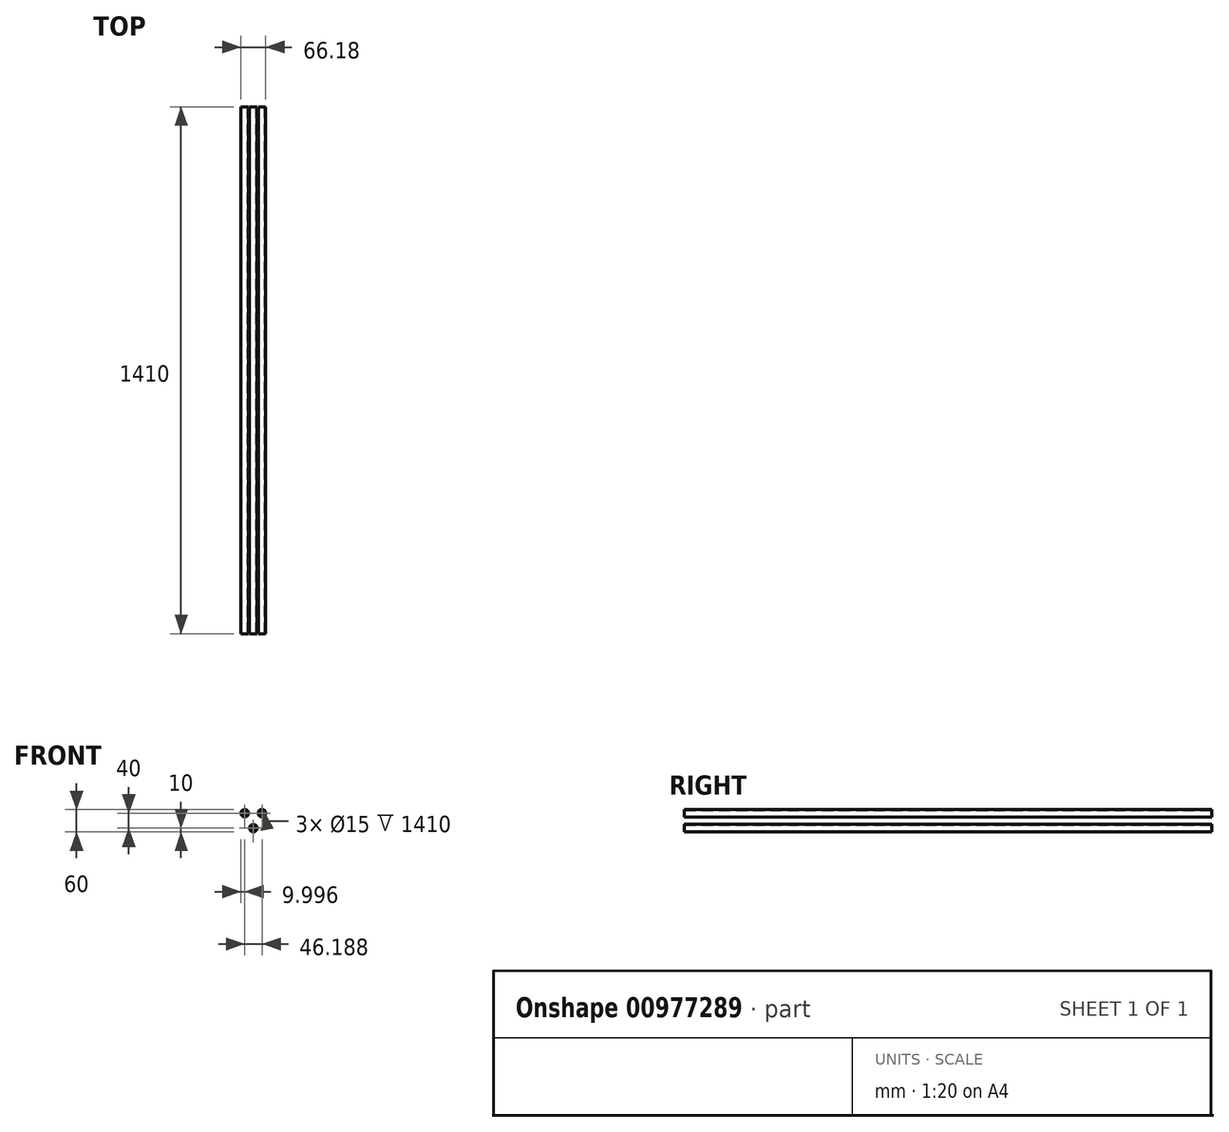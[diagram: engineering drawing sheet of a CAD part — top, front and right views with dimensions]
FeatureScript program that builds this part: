
annotation { "Feature Type Name" : "Feature", "Feature Type Description" : "" }
export const myFeature = defineFeature(function(context is Context, id is Id, definition is map)
    precondition{}
    {
        {
            var Q0;
            Q0=qCreatedBy(makeId("Front.planeOp"),FACE);
            var sketch = newSketch(context, id + "F0", { "sketchPlane" : qUnion([Q0])});
            skCircle(sketch, "E0", {"center": v(0, 0) * mm, "radius": 10 * mm});
            skCircle(sketch, "E1", {"center": v(23.1, 40) * mm, "radius": 10 * mm});
            skCircle(sketch, "E2", {"center": v(-23.1, 40) * mm, "radius": 10 * mm});
            skCircle(sketch, "E3", {"center": v(-23.1, 40) * mm, "radius": 15 * mm});
            skCircle(sketch, "E4", {"center": v(23.1, 40) * mm, "radius": 15 * mm});
            skCircle(sketch, "E5", {"center": v(0, 0) * mm, "radius": 15 * mm});
            skLineSegment(sketch, "E6", {"start": v(0, 0) * mm, "end": v(-23.1, 40) * mm});
            skLineSegment(sketch, "E7", {"start": v(23.1, 40) * mm, "end": v(0, 0) * mm});
            skLineSegment(sketch, "E8", {"start": v(-23.1, 40) * mm, "end": v(23.1, 40) * mm});
            skCircle(sketch, "E9", {"center": v(-23.1, 40) * mm, "radius": 7.5 * mm});
            skCircle(sketch, "E10", {"center": v(23.1, 40) * mm, "radius": 7.5 * mm});
            skCircle(sketch, "E11", {"center": v(0, 0) * mm, "radius": 7.5 * mm});
            skSolve(sketch);
        }
        {
            var Q0;
            {var subQ0=sQuery(id+"F0.wireOp",EDGE,"E6");var subQ1=sQuery(id+"F0.wireOp",EDGE,"E2");var subQ2=makeQuery(id+"F0.imprint","INTERSECT",VERTEX,{"derivedFrom":[subQ1,subQ0]});Q0=makeQuery(id+"F0.imprint","IMPRINT",FACE,{"disambiguationData":[TD([[makeQuery(id+"F0.imprint","IMPRINT",EDGE,{"disambiguationData":[TD([[subQ2,1.0]])],"derivedFrom":subQ1}),1.0]])]});}
            var Q1;
            {var subQ0=sQuery(id+"F0.wireOp",EDGE,"E6");var subQ1=sQuery(id+"F0.wireOp",EDGE,"E2");var subQ2=makeQuery(id+"F0.imprint","INTERSECT",VERTEX,{"derivedFrom":[subQ1,subQ0]});Q1=makeQuery(id+"F0.imprint","IMPRINT",FACE,{"disambiguationData":[TD([[makeQuery(id+"F0.imprint","IMPRINT",EDGE,{"disambiguationData":[TD([[subQ2,-1.0]])],"derivedFrom":subQ1}),1.0]])]});}
            var Q2;
            {var subQ0=sQuery(id+"F0.wireOp",EDGE,"E7");var subQ1=sQuery(id+"F0.wireOp",EDGE,"E1");var subQ2=makeQuery(id+"F0.imprint","INTERSECT",VERTEX,{"derivedFrom":[subQ1,subQ0]});Q2=makeQuery(id+"F0.imprint","IMPRINT",FACE,{"disambiguationData":[TD([[makeQuery(id+"F0.imprint","IMPRINT",EDGE,{"disambiguationData":[TD([[subQ2,-1.0]])],"derivedFrom":subQ1}),1.0]])]});}
            var Q3;
            {var subQ0=sQuery(id+"F0.wireOp",EDGE,"E7");var subQ1=sQuery(id+"F0.wireOp",EDGE,"E1");var subQ2=makeQuery(id+"F0.imprint","INTERSECT",VERTEX,{"derivedFrom":[subQ1,subQ0]});Q3=makeQuery(id+"F0.imprint","IMPRINT",FACE,{"disambiguationData":[TD([[makeQuery(id+"F0.imprint","IMPRINT",EDGE,{"disambiguationData":[TD([[subQ2,1.0]])],"derivedFrom":subQ1}),1.0]])]});}
            var Q4;
            {var subQ0=sQuery(id+"F0.wireOp",EDGE,"E6");var subQ1=sQuery(id+"F0.wireOp",EDGE,"E0");var subQ2=makeQuery(id+"F0.imprint","INTERSECT",VERTEX,{"derivedFrom":[subQ1,subQ0]});Q4=makeQuery(id+"F0.imprint","IMPRINT",FACE,{"disambiguationData":[TD([[makeQuery(id+"F0.imprint","IMPRINT",EDGE,{"disambiguationData":[TD([[subQ2,1.0]])],"derivedFrom":subQ1}),1.0]])]});}
            var Q5;
            {var subQ0=sQuery(id+"F0.wireOp",EDGE,"E6");var subQ1=sQuery(id+"F0.wireOp",EDGE,"E0");var subQ2=makeQuery(id+"F0.imprint","INTERSECT",VERTEX,{"derivedFrom":[subQ1,subQ0]});Q5=makeQuery(id+"F0.imprint","IMPRINT",FACE,{"disambiguationData":[TD([[makeQuery(id+"F0.imprint","IMPRINT",EDGE,{"disambiguationData":[TD([[subQ2,-1.0]])],"derivedFrom":subQ1}),1.0]])]});}
            extrude(context, id + "F1", {"entities" : qUnion([Q0, Q1, Q2, Q3, Q4, Q5]), "depth" : 1410 * mm, "offsetDistance" : 25 * mm});
        }
    });
